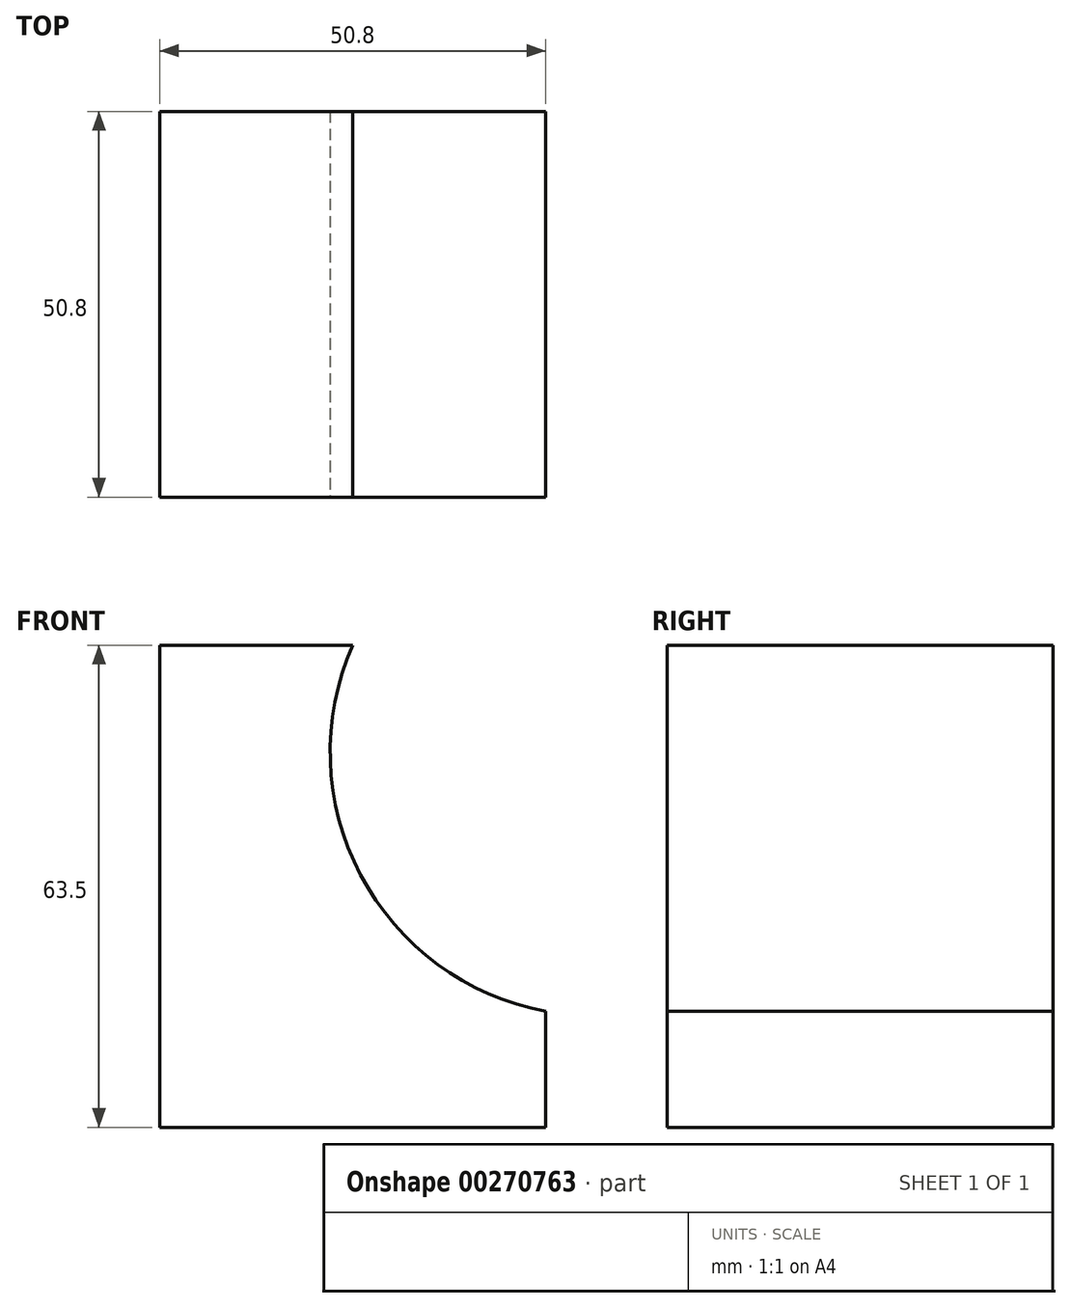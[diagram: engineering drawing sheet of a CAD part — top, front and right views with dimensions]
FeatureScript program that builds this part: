
annotation { "Feature Type Name" : "Feature", "Feature Type Description" : "" }
export const myFeature = defineFeature(function(context is Context, id is Id, definition is map)
    precondition{}
    {
        {
            var Q0;
            Q0=qCreatedBy(makeId("Front.planeOp"),FACE);
            var sketch = newSketch(context, id + "F0", { "sketchPlane" : qUnion([Q0])});
            skLineSegment(sketch, "E0", {"start": v(0, 0) * mm, "end": v(-50.8, 0) * mm});
            skLineSegment(sketch, "E1", {"start": v(-50.8, 0) * mm, "end": v(-50.8, 63.5) * mm});
            skLineSegment(sketch, "E2", {"start": v(-50.8, 63.5) * mm, "end": v(-25.4, 63.5) * mm});
            skLineSegment(sketch, "E3", {"start": v(-25.4, 63.5) * mm, "end": v(-25.4, 38.1) * mm});
            skLineSegment(sketch, "E4", {"start": v(-25.4, 38.1) * mm, "end": v(0, 38.1) * mm});
            skLineSegment(sketch, "E5", {"start": v(0, 38.1) * mm, "end": v(0, 0) * mm});
            skSolve(sketch);
        }
        {
            var Q0;
            Q0 = qSketchRegion(id + "F0", true);
            extrude(context, id + "F1", {"entities" : qUnion([Q0]), "depth" : 50.8 * mm});
        }
        {
            var Q0;
            Q0=makeQuery(id+"F1.opExtrude","CAP_FACE",FACE,{"disambiguationData":[OSD([sQuery(id+"F0.wireOp",EDGE,"E0"),sQuery(id+"F0.wireOp",EDGE,"E1"),sQuery(id+"F0.wireOp",EDGE,"E2"),sQuery(id+"F0.wireOp",EDGE,"E3"),sQuery(id+"F0.wireOp",EDGE,"E4"),sQuery(id+"F0.wireOp",EDGE,"E5")])],"isStart":false});
            var sketch = newSketch(context, id + "F2", { "sketchPlane" : qUnion([Q0])});
            skArc(sketch, "E6", {"start": v(-25.4, 63.5) * mm, "mid": v(-24.36, 33.25) * mm, "end": v(0, 15.28) * mm});
            skSolve(sketch);
        }
        {
            var Q0;
            {var subQ0=sQuery(id+"F2.wireOp",EDGE,"E6");Q0=makeQuery(id+"F2.imprint","IMPRINT",FACE,{"disambiguationData":[TD([[makeQuery(id+"F2.imprint","IMPRINT",EDGE,{"derivedFrom":subQ0}),1.0]])]});}
            extrude(context, id + "F3", {"entities" : qUnion([Q0]), "operationType" : NewBodyOperationType.REMOVE, "oppositeDirection" : true, "depth" : 50.8 * mm});
        }
    });
